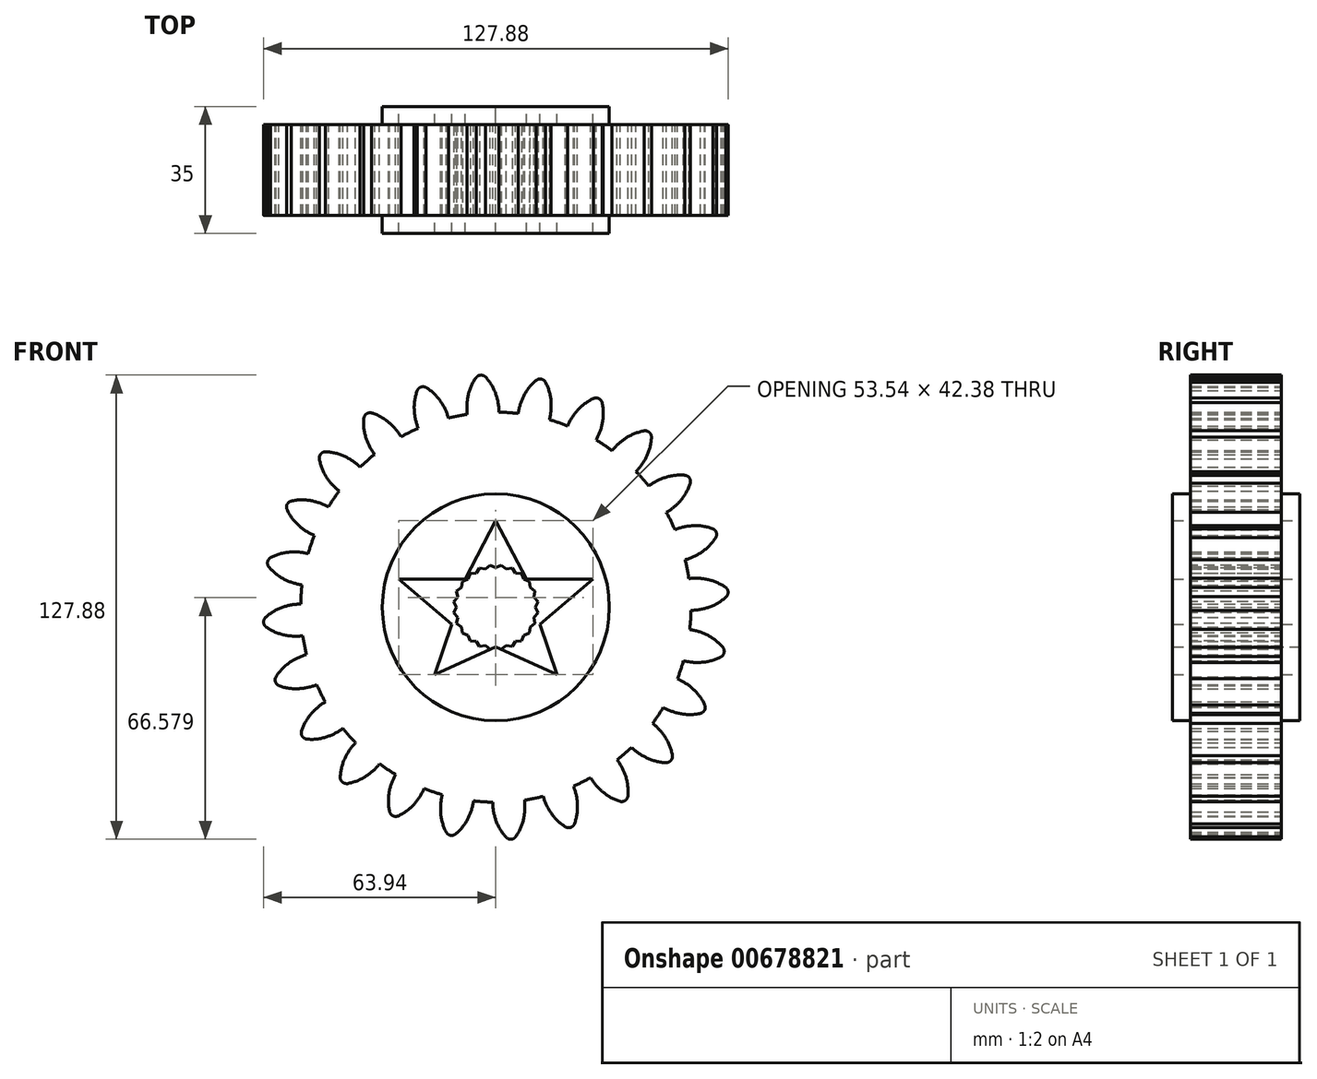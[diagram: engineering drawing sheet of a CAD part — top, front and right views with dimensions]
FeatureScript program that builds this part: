
annotation { "Feature Type Name" : "Feature", "Feature Type Description" : "" }
export const myFeature = defineFeature(function(context is Context, id is Id, definition is map)
    precondition{}
    {
        {
            var Q0;
            Q0=qCreatedBy(makeId("Front.planeOp"),FACE);
            var sketch = newSketch(context, id + "F0", { "sketchPlane" : qUnion([Q0])});
            skCircle(sketch, "E0", {"center": v(0, 0) * mm, "radius": 53.72 * mm});
            skCircle(sketch, "E1", {"center": v(0, 0) * mm, "radius": 58.67 * mm, "construction": true});
            skCircle(sketch, "E2", {"center": v(0, 0) * mm, "radius": 63.5 * mm, "construction": true});
            skLineSegment(sketch, "E3", {"start": v(0, 0) * mm, "end": v(0, 90.28) * mm, "construction": true});
            skLineSegment(sketch, "E4", {"start": v(0, 0) * mm, "end": v(-5.89, 89.83) * mm, "construction": true});
            skLineSegment(sketch, "E5", {"start": v(0, 58.67) * mm, "end": v(-86.47, 27.2) * mm, "construction": true});
            skLineSegment(sketch, "E6", {"start": v(0, 58.67) * mm, "end": v(-89.07, 58.67) * mm, "construction": true});
            skCircle(sketch, "E7", {"center": v(0, 0) * mm, "radius": 55.14 * mm, "construction": true});
            skCircle(sketch, "E8", {"center": v(0, 58.67) * mm, "radius": 14.6 * mm, "construction": true});
            skCircle(sketch, "E9", {"center": v(-13.72, 53.68) * mm, "radius": 14.6 * mm, "construction": true});
            skArc(sketch, "E10", {"start": v(0, 58.67) * mm, "mid": v(-1.18, 61.2) * mm, "end": v(-2.86, 63.44) * mm});
            skArc(sketch, "E11", {"start": v(0.88, 53.71) * mm, "mid": v(0.64, 56.23) * mm, "end": v(0, 58.67) * mm});
            skArc(sketch, "E12.MirrorCS", {"start": v(-7.88, 53.14) * mm, "mid": v(-7.97, 55.66) * mm, "end": v(-7.66, 58.17) * mm});
            skArc(sketch, "E13.MirrorCS", {"start": v(-7.66, 58.17) * mm, "mid": v(-6.82, 60.83) * mm, "end": v(-5.45, 63.27) * mm});
            skArc(sketch, "E14", {"start": v(-2.86, 63.44) * mm, "mid": v(-4.2, 63.93) * mm, "end": v(-5.45, 63.27) * mm});
            skCircle(sketch, "E15", {"center": v(0, 0) * mm, "radius": 31.25 * mm});
            skLineSegment(sketch, "E16", {"start": v(0, 23.83) * mm, "end": v(8.38, 7.72) * mm});
            skLineSegment(sketch, "E17", {"start": v(8.38, 7.72) * mm, "end": v(26.77, 7.72) * mm});
            skLineSegment(sketch, "E18", {"start": v(26.77, 7.72) * mm, "end": v(12.19, -4.72) * mm});
            skLineSegment(sketch, "E19", {"start": v(12.19, -4.72) * mm, "end": v(16.83, -18.55) * mm});
            skLineSegment(sketch, "E20", {"start": v(16.83, -18.55) * mm, "end": v(0, -10.88) * mm});
            skLineSegment(sketch, "E21.MirrorCS", {"start": v(0, 23.83) * mm, "end": v(-8.38, 7.72) * mm});
            skLineSegment(sketch, "E22.MirrorCS", {"start": v(-8.38, 7.72) * mm, "end": v(-26.77, 7.72) * mm});
            skLineSegment(sketch, "E23.MirrorCS", {"start": v(-26.77, 7.72) * mm, "end": v(-12.19, -4.72) * mm});
            skLineSegment(sketch, "E24.MirrorCS", {"start": v(-12.19, -4.72) * mm, "end": v(-16.83, -18.55) * mm});
            skLineSegment(sketch, "E25.MirrorCS", {"start": v(-16.83, -18.55) * mm, "end": v(0, -10.88) * mm});
            skSolve(sketch);
        }
        {
            var Q0;
            {var subQ0=sQuery(id+"F0.wireOp",EDGE,"E0");var subQ1=makeQuery(id+"F0.imprint","INTERSECT",VERTEX,{"derivedFrom":[subQ0,sQuery(id+"F0.wireOp",EDGE,"E12.MirrorCS")]});Q0=makeQuery(id+"F0.imprint","IMPRINT",FACE,{"disambiguationData":[TD([[makeQuery(id+"F0.imprint","IMPRINT",EDGE,{"disambiguationData":[TD([[subQ1,1.0]])],"derivedFrom":subQ0}),1.0]])]});}
            var Q1;
            Q1=makeQuery(id+"F0.imprint","IMPRINT",FACE,{"disambiguationData":[TD([[makeQuery(id+"F0.imprint","IMPRINT",EDGE,{"derivedFrom":sQuery(id+"F0.wireOp",EDGE,"E10")}),1.0]])]});
            var Q2;
            Q2=makeQuery(id+"F0.imprint","IMPRINT",FACE,{"disambiguationData":[TD([[makeQuery(id+"F0.imprint","IMPRINT",EDGE,{"derivedFrom":sQuery(id+"F0.wireOp",EDGE,"E15")}),1.0]])]});
            extrude(context, id + "F1", {"entities" : qUnion([Q0, Q1, Q2]), "endBound" : BoundingType.SYMMETRIC, "depth" : 25 * mm, "offsetDistance" : 25 * mm});
        }
        {
            var Q0;
            Q0=makeQuery(id+"F1.opExtrude","SWEPT_BODY",BODY,{"disambiguationData":[OSD([sQuery(id+"F0.wireOp",EDGE,"E0"),sQuery(id+"F0.wireOp",EDGE,"E10"),sQuery(id+"F0.wireOp",EDGE,"E12.MirrorCS"),sQuery(id+"F0.wireOp",EDGE,"E13.MirrorCS"),sQuery(id+"F0.wireOp",EDGE,"E11"),sQuery(id+"F0.wireOp",EDGE,"E14")])]});
            var Q1;
            Q1=makeQuery(id+"F1.opExtrude","SWEPT_FACE",FACE,{"disambiguationData":[OSD([sQuery(id+"F0.wireOp",EDGE,"E0")])]});
            circularPattern(context, id + "F2", {"entities" : qUnion([Q0]), "axis" : qUnion([Q1]), "angle" : 360 * degree, "instanceCount" : 24, "equalSpace" : true});
        }
        {
            var Q0;
            Q0=makeQuery(id+"F0.imprint","IMPRINT",FACE,{"disambiguationData":[TD([[makeQuery(id+"F0.imprint","IMPRINT",EDGE,{"derivedFrom":sQuery(id+"F0.wireOp",EDGE,"E15")}),1.0]])]});
            extrude(context, id + "F3", {"entities" : qUnion([Q0]), "operationType" : NewBodyOperationType.ADD, "endBound" : BoundingType.SYMMETRIC, "depth" : 35 * mm, "offsetDistance" : 25 * mm});
        }
    });
